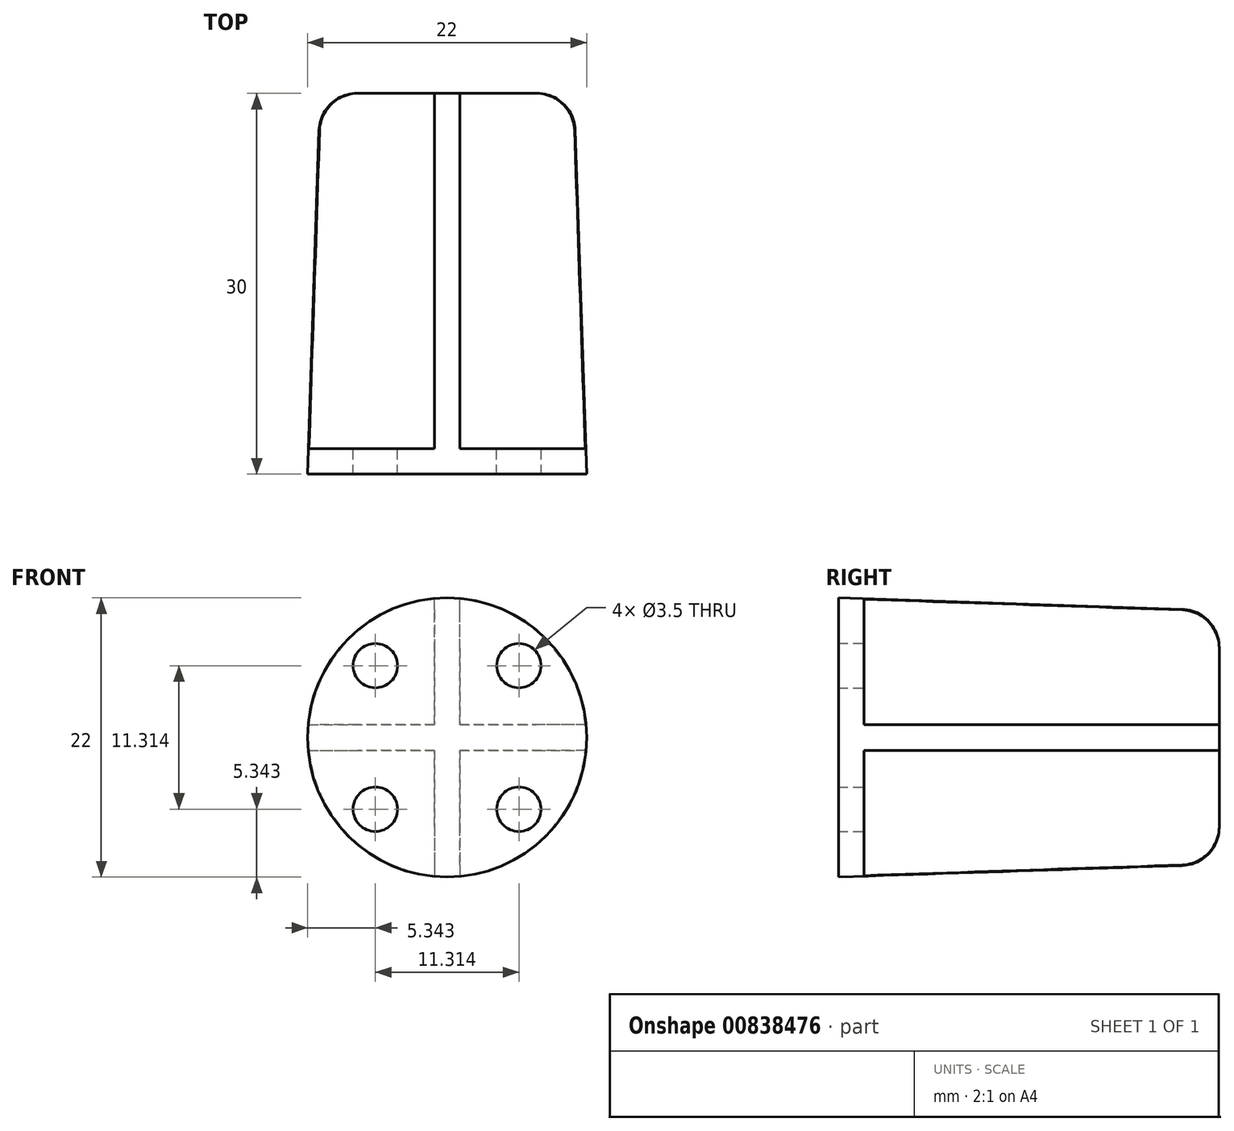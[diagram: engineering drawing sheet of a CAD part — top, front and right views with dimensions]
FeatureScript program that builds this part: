
annotation { "Feature Type Name" : "Feature", "Feature Type Description" : "" }
export const myFeature = defineFeature(function(context is Context, id is Id, definition is map)
    precondition{}
    {
        {
            var Q0;
            Q0=qCreatedBy(makeId("Top.planeOp"),FACE);
            var sketch = newSketch(context, id + "F0", { "sketchPlane" : qUnion([Q0])});
            skLineSegment(sketch, "E0", {"start": v(0, 0) * mm, "end": v(0, 30) * mm});
            skLineSegment(sketch, "E1", {"start": v(0, 30) * mm, "end": v(10, 30) * mm});
            skLineSegment(sketch, "E2", {"start": v(10, 30) * mm, "end": v(11, 0) * mm});
            skLineSegment(sketch, "E3", {"start": v(11, 0) * mm, "end": v(0, 0) * mm});
            skSolve(sketch);
        }
        {
            var Q0;
            Q0=makeQuery(id+"F0.imprint","IMPRINT",FACE,{"disambiguationData":[TD([[makeQuery(id+"F0.imprint","IMPRINT",EDGE,{"derivedFrom":sQuery(id+"F0.wireOp",EDGE,"E0")}),-1.0]])]});
            var Q1;
            Q1=sQuery(id+"F0.wireOp",EDGE,"E1");
            var Q2;
            Q2=sQuery(id+"F0.wireOp",EDGE,"E2");
            var Q3;
            Q3=sQuery(id+"F0.wireOp",EDGE,"E3");
            var Q4;
            Q4=sQuery(id+"F0.wireOp",EDGE,"E0");
            var Q5;
            Q5=sQuery(id+"F0.wireOp",EDGE,"E0");
            revolve(context, id + "F1", {"surfaceOperationType" : NewSurfaceOperationType.NEW, "entities" : qUnion([Q0]), "surfaceEntities" : qUnion([Q1, Q2, Q3, Q4]), "axis" : qUnion([Q5]), "revolveType" : RevolveType.FULL});
        }
        {
            var Q0;
            Q0=makeQuery(id+"F1.opRevolve","SWEPT_FACE",FACE,{"disambiguationData":[OSD([sQuery(id+"F0.wireOp",EDGE,"E1")])]});
            var sketch = newSketch(context, id + "F2", { "sketchPlane" : qUnion([Q0])});
            skLineSegment(sketch, "E4", {"start": v(0, 20) * mm, "end": v(0, -20) * mm, "construction": true});
            skLineSegment(sketch, "E5", {"start": v(-20, 0) * mm, "end": v(20, 0) * mm, "construction": true});
            skLineSegment(sketch, "E6", {"start": v(1.01, 20) * mm, "end": v(1.01, 1) * mm});
            skLineSegment(sketch, "E7", {"start": v(1.01, 1) * mm, "end": v(21.01, 1.01) * mm});
            skLineSegment(sketch, "E8", {"start": v(21.01, 1.01) * mm, "end": v(21.01, 20) * mm});
            skLineSegment(sketch, "E9", {"start": v(21.01, 20) * mm, "end": v(1.01, 20) * mm});
            skLineSegment(sketch, "E10.MirrorCS", {"start": v(-1.01, 20) * mm, "end": v(-1.01, 1) * mm});
            skLineSegment(sketch, "E11.MirrorCS", {"start": v(-1.01, 1) * mm, "end": v(-21.01, 1.01) * mm});
            skLineSegment(sketch, "E12.MirrorCS", {"start": v(-21.01, 1.01) * mm, "end": v(-21.01, 20) * mm});
            skLineSegment(sketch, "E13.MirrorCS", {"start": v(-21.01, 20) * mm, "end": v(-1.01, 20) * mm});
            skLineSegment(sketch, "E14.MirrorCS", {"start": v(1.01, -1) * mm, "end": v(21.01, -1.01) * mm});
            skLineSegment(sketch, "E15.MirrorCS", {"start": v(1.01, -20) * mm, "end": v(1.01, -1) * mm});
            skLineSegment(sketch, "E16.MirrorCS", {"start": v(21.01, -20) * mm, "end": v(1.01, -20) * mm});
            skLineSegment(sketch, "E17.MirrorCS", {"start": v(21.01, -1.01) * mm, "end": v(21.01, -20) * mm});
            skLineSegment(sketch, "E18.MirrorCS", {"start": v(-1.01, -1) * mm, "end": v(-21.01, -1.01) * mm});
            skLineSegment(sketch, "E19.MirrorCS", {"start": v(-21.01, -1.01) * mm, "end": v(-21.01, -20) * mm});
            skLineSegment(sketch, "E20.MirrorCS", {"start": v(-21.01, -20) * mm, "end": v(-1.01, -20) * mm});
            skLineSegment(sketch, "E21.MirrorCS", {"start": v(-1.01, -20) * mm, "end": v(-1.01, -1) * mm});
            skSolve(sketch);
        }
        {
            var Q0;
            Q0 = qSketchRegion(id + "F2", true);
            var Q1;
            Q1=makeQuery(id+"F1.opRevolve","SWEPT_FACE",FACE,{"disambiguationData":[OSD([sQuery(id+"F0.wireOp",EDGE,"E3")])]});
            extrude(context, id + "F3", {"entities" : qUnion([Q0]), "operationType" : NewBodyOperationType.REMOVE, "endBound" : BoundingType.UP_TO_SURFACE, "oppositeDirection" : true, "depth" : 25 * mm, "endBoundEntityFace" : qUnion([Q1]), "hasOffset" : true, "offsetDistance" : 2 * mm});
        }
        {
            var Q0;
            {var subQ0=sQuery(id+"F0.wireOp",EDGE,"E1");var subQ1=sQuery(id+"F0.wireOp",EDGE,"E2");Q0=makeQuery(id+"F3.boolean.opBoolean","SPLIT",EDGE,{"disambiguationData":[TD([makeQuery(id+"F3.opExtrude","SWEPT_FACE",FACE,{"disambiguationData":[OSD([sQuery(id+"F2.wireOp",EDGE,"E11.MirrorCS")])]})])],"derivedFrom":makeQuery(id+"F1.opRevolve","SWEPT_EDGE",EDGE,{"disambiguationData":[OSD([subQ0,subQ1])]})});}
            var Q1;
            {var subQ0=sQuery(id+"F0.wireOp",EDGE,"E1");var subQ1=sQuery(id+"F0.wireOp",EDGE,"E2");Q1=makeQuery(id+"F3.boolean.opBoolean","SPLIT",EDGE,{"disambiguationData":[TD([makeQuery(id+"F3.opExtrude","SWEPT_FACE",FACE,{"disambiguationData":[OSD([sQuery(id+"F2.wireOp",EDGE,"E6")])]})])],"derivedFrom":makeQuery(id+"F1.opRevolve","SWEPT_EDGE",EDGE,{"disambiguationData":[OSD([subQ0,subQ1])]})});}
            var Q2;
            {var subQ0=sQuery(id+"F0.wireOp",EDGE,"E1");var subQ1=sQuery(id+"F0.wireOp",EDGE,"E2");Q2=makeQuery(id+"F3.boolean.opBoolean","SPLIT",EDGE,{"disambiguationData":[TD([makeQuery(id+"F3.opExtrude","SWEPT_FACE",FACE,{"disambiguationData":[OSD([sQuery(id+"F2.wireOp",EDGE,"E7")])]})])],"derivedFrom":makeQuery(id+"F1.opRevolve","SWEPT_EDGE",EDGE,{"disambiguationData":[OSD([subQ0,subQ1])]})});}
            var Q3;
            {var subQ0=sQuery(id+"F0.wireOp",EDGE,"E1");var subQ1=sQuery(id+"F0.wireOp",EDGE,"E2");Q3=makeQuery(id+"F3.boolean.opBoolean","SPLIT",EDGE,{"disambiguationData":[TD([makeQuery(id+"F3.opExtrude","SWEPT_FACE",FACE,{"disambiguationData":[OSD([sQuery(id+"F2.wireOp",EDGE,"E15.MirrorCS")])]})])],"derivedFrom":makeQuery(id+"F1.opRevolve","SWEPT_EDGE",EDGE,{"disambiguationData":[OSD([subQ0,subQ1])]})});}
            fillet(context, id + "F4", {"entities" : qUnion([Q0, Q1, Q2, Q3]), "radius" : 3 * mm, "tangentPropagation" : true, "allowEdgeOverflow" : false});
        }
        {
            var Q0;
            Q0=makeQuery(id+"F3.boolean.opBoolean","COPY",FACE,{"derivedFrom":makeQuery(id+"F3.opExtrude","CAP_FACE",FACE,{"disambiguationData":[OSD([sQuery(id+"F2.wireOp",EDGE,"E10.MirrorCS"),sQuery(id+"F2.wireOp",EDGE,"E11.MirrorCS"),sQuery(id+"F2.wireOp",EDGE,"E12.MirrorCS"),sQuery(id+"F2.wireOp",EDGE,"E13.MirrorCS")])],"isStart":false})});
            var sketch = newSketch(context, id + "F5", { "sketchPlane" : qUnion([Q0])});
            skCircle(sketch, "E22", {"center": v(-5.66, 5.66) * mm, "radius": 1.75 * mm});
            skCircle(sketch, "E23", {"center": v(5.66, -5.66) * mm, "radius": 1.75 * mm});
            skLineSegment(sketch, "E24", {"start": v(0, 0) * mm, "end": v(7.73, -7.73) * mm, "construction": true});
            skLineSegment(sketch, "E25", {"start": v(13.08, 0) * mm, "end": v(-12.68, 0) * mm, "construction": true});
            skCircle(sketch, "E26.MirrorC", {"center": v(-5.66, -5.66) * mm, "radius": 1.75 * mm});
            skCircle(sketch, "E27.MirrorC", {"center": v(5.66, 5.66) * mm, "radius": 1.75 * mm});
            skSolve(sketch);
        }
        {
            var Q0;
            Q0 = qSketchRegion(id + "F5", true);
            extrude(context, id + "F6", {"entities" : qUnion([Q0]), "operationType" : NewBodyOperationType.REMOVE, "oppositeDirection" : true, "depth" : 25 * mm, "offsetDistance" : 25 * mm});
        }
    });
